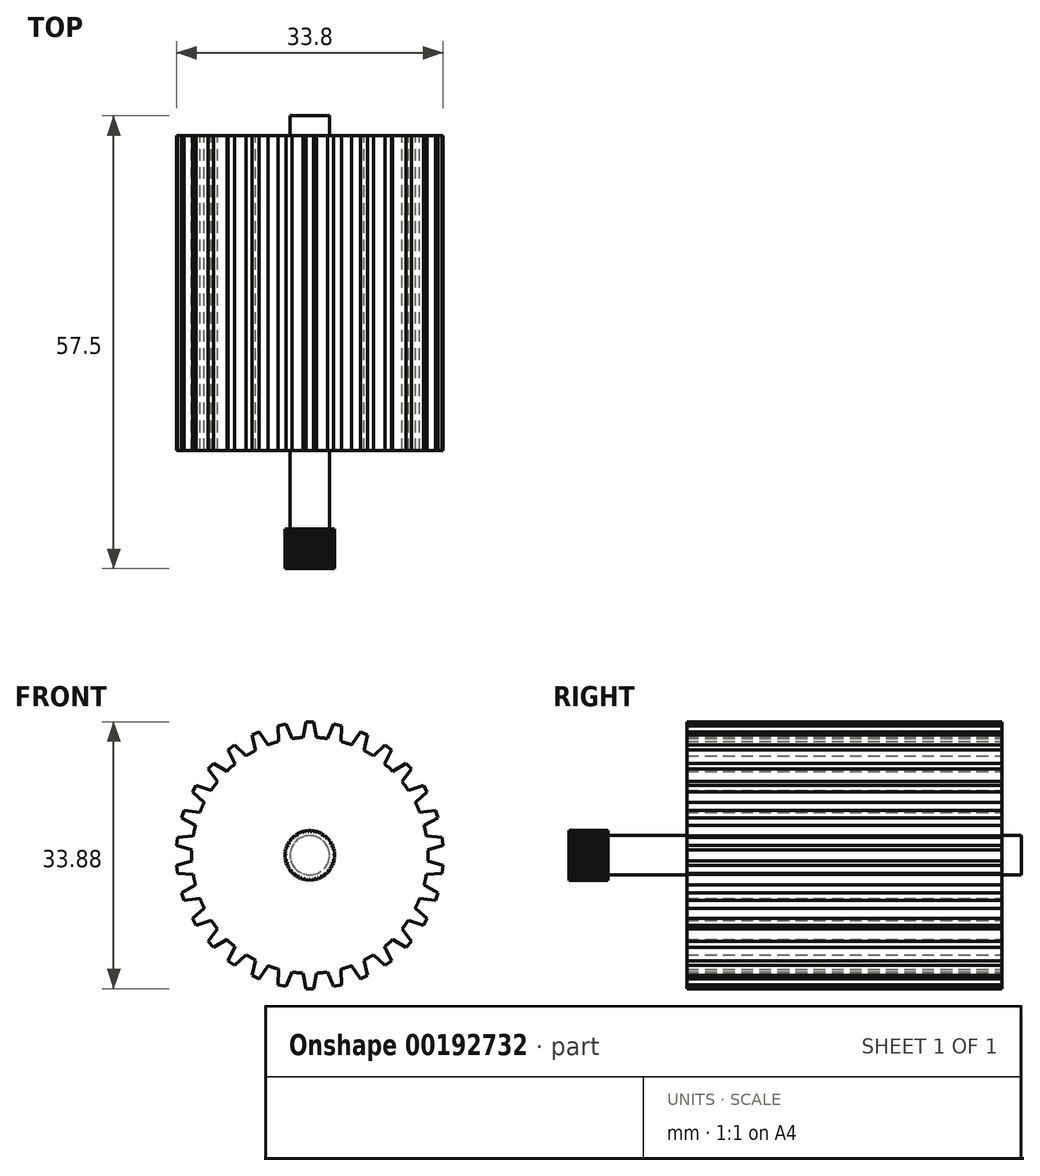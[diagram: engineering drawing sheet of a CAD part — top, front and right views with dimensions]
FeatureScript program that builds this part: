
annotation { "Feature Type Name" : "Feature", "Feature Type Description" : "" }
export const myFeature = defineFeature(function(context is Context, id is Id, definition is map)
    precondition{}
    {
        {
            var Q0;
            Q0=qCreatedBy(makeId("Front.planeOp"),FACE);
            var sketch = newSketch(context, id + "F0", { "sketchPlane" : qUnion([Q0])});
            skCircle(sketch, "E0", {"center": v(0, 0) * mm, "radius": 15 * mm});
            skLineSegment(sketch, "E1", {"start": v(0, 0) * mm, "end": v(0, 16.94) * mm, "construction": true});
            skLineSegment(sketch, "E2", {"start": v(0, 16.94) * mm, "end": v(-0.5, 16.94) * mm});
            skLineSegment(sketch, "E3", {"start": v(-0.5, 16.94) * mm, "end": v(-0.88, 14.97) * mm});
            skLineSegment(sketch, "E4.MirrorCS", {"start": v(0, 16.94) * mm, "end": v(0.5, 16.94) * mm});
            skLineSegment(sketch, "E5.MirrorCS", {"start": v(0.5, 16.94) * mm, "end": v(0.88, 14.97) * mm});
            skLineSegment(sketch, "E6.1.0", {"start": v(-4.01, 16.46) * mm, "end": v(-3.98, 14.46) * mm});
            skLineSegment(sketch, "E6.1.1", {"start": v(-3.52, 16.57) * mm, "end": v(-4.01, 16.46) * mm});
            skLineSegment(sketch, "E6.1.2", {"start": v(-3.52, 16.57) * mm, "end": v(-3.03, 16.67) * mm});
            skLineSegment(sketch, "E6.1.3", {"start": v(-3.03, 16.67) * mm, "end": v(-2.25, 14.83) * mm});
            skLineSegment(sketch, "E6.2.0", {"start": v(-7.35, 15.27) * mm, "end": v(-6.9, 13.32) * mm});
            skLineSegment(sketch, "E6.2.1", {"start": v(-6.89, 15.47) * mm, "end": v(-7.35, 15.27) * mm});
            skLineSegment(sketch, "E6.2.2", {"start": v(-6.89, 15.47) * mm, "end": v(-6.43, 15.68) * mm});
            skLineSegment(sketch, "E6.2.3", {"start": v(-6.43, 15.68) * mm, "end": v(-5.28, 14.04) * mm});
            skLineSegment(sketch, "E7.2.3.0", {"start": v(-10.36, 13.4) * mm, "end": v(-9.52, 11.6) * mm});
            skLineSegment(sketch, "E7.3.3.0", {"start": v(-9.96, 13.7) * mm, "end": v(-10.36, 13.4) * mm});
            skLineSegment(sketch, "E7.6.3.0", {"start": v(-9.96, 13.7) * mm, "end": v(-9.55, 14) * mm});
            skLineSegment(sketch, "E7.9.3.0", {"start": v(-9.55, 14) * mm, "end": v(-8.09, 12.63) * mm});
            skLineSegment(sketch, "E7.2.4.0", {"start": v(-12.92, 10.96) * mm, "end": v(-11.72, 9.36) * mm});
            skLineSegment(sketch, "E7.3.4.0", {"start": v(-12.59, 11.33) * mm, "end": v(-12.92, 10.96) * mm});
            skLineSegment(sketch, "E7.6.4.0", {"start": v(-12.59, 11.33) * mm, "end": v(-12.25, 11.7) * mm});
            skLineSegment(sketch, "E7.9.4.0", {"start": v(-12.25, 11.7) * mm, "end": v(-10.54, 10.68) * mm});
            skLineSegment(sketch, "E7.2.5.0", {"start": v(-14.92, 8.04) * mm, "end": v(-13.4, 6.72) * mm});
            skLineSegment(sketch, "E7.3.5.0", {"start": v(-14.67, 8.47) * mm, "end": v(-14.92, 8.04) * mm});
            skLineSegment(sketch, "E7.6.5.0", {"start": v(-14.67, 8.47) * mm, "end": v(-14.42, 8.9) * mm});
            skLineSegment(sketch, "E7.9.5.0", {"start": v(-14.42, 8.9) * mm, "end": v(-12.53, 8.25) * mm});
            skLineSegment(sketch, "E7.2.6.0", {"start": v(-16.26, 4.76) * mm, "end": v(-14.51, 3.79) * mm});
            skLineSegment(sketch, "E7.3.6.0", {"start": v(-16.1, 5.23) * mm, "end": v(-16.26, 4.76) * mm});
            skLineSegment(sketch, "E7.6.6.0", {"start": v(-16.1, 5.23) * mm, "end": v(-15.95, 5.7) * mm});
            skLineSegment(sketch, "E7.9.6.0", {"start": v(-15.95, 5.7) * mm, "end": v(-13.97, 5.47) * mm});
            skLineSegment(sketch, "E7.2.7.0", {"start": v(-16.9, 1.27) * mm, "end": v(-14.98, 0.69) * mm});
            skLineSegment(sketch, "E7.3.7.0", {"start": v(-16.84, 1.77) * mm, "end": v(-16.9, 1.27) * mm});
            skLineSegment(sketch, "E7.6.7.0", {"start": v(-16.84, 1.77) * mm, "end": v(-16.8, 2.27) * mm});
            skLineSegment(sketch, "E7.9.7.0", {"start": v(-16.8, 2.27) * mm, "end": v(-14.8, 2.44) * mm});
            skLineSegment(sketch, "E7.2.8.0", {"start": v(-16.8, -2.27) * mm, "end": v(-14.8, -2.44) * mm});
            skLineSegment(sketch, "E7.3.8.0", {"start": v(-16.84, -1.77) * mm, "end": v(-16.8, -2.27) * mm});
            skLineSegment(sketch, "E7.6.8.0", {"start": v(-16.84, -1.77) * mm, "end": v(-16.9, -1.27) * mm});
            skLineSegment(sketch, "E7.9.8.0", {"start": v(-16.9, -1.27) * mm, "end": v(-14.98, -0.69) * mm});
            skLineSegment(sketch, "E7.2.9.0", {"start": v(-15.95, -5.7) * mm, "end": v(-13.97, -5.47) * mm});
            skLineSegment(sketch, "E7.3.9.0", {"start": v(-16.1, -5.23) * mm, "end": v(-15.95, -5.7) * mm});
            skLineSegment(sketch, "E7.6.9.0", {"start": v(-16.1, -5.23) * mm, "end": v(-16.26, -4.76) * mm});
            skLineSegment(sketch, "E7.9.9.0", {"start": v(-16.26, -4.76) * mm, "end": v(-14.51, -3.79) * mm});
            skLineSegment(sketch, "E7.2.10.0", {"start": v(-14.42, -8.9) * mm, "end": v(-12.53, -8.25) * mm});
            skLineSegment(sketch, "E7.3.10.0", {"start": v(-14.67, -8.47) * mm, "end": v(-14.42, -8.9) * mm});
            skLineSegment(sketch, "E7.6.10.0", {"start": v(-14.67, -8.47) * mm, "end": v(-14.92, -8.04) * mm});
            skLineSegment(sketch, "E7.9.10.0", {"start": v(-14.92, -8.04) * mm, "end": v(-13.4, -6.72) * mm});
            skLineSegment(sketch, "E7.2.11.0", {"start": v(-12.25, -11.7) * mm, "end": v(-10.54, -10.68) * mm});
            skLineSegment(sketch, "E7.3.11.0", {"start": v(-12.59, -11.33) * mm, "end": v(-12.25, -11.7) * mm});
            skLineSegment(sketch, "E7.6.11.0", {"start": v(-12.59, -11.33) * mm, "end": v(-12.92, -10.96) * mm});
            skLineSegment(sketch, "E7.9.11.0", {"start": v(-12.92, -10.96) * mm, "end": v(-11.72, -9.36) * mm});
            skLineSegment(sketch, "E7.2.12.0", {"start": v(-9.55, -14) * mm, "end": v(-8.09, -12.63) * mm});
            skLineSegment(sketch, "E7.3.12.0", {"start": v(-9.96, -13.7) * mm, "end": v(-9.55, -14) * mm});
            skLineSegment(sketch, "E7.6.12.0", {"start": v(-9.96, -13.7) * mm, "end": v(-10.36, -13.4) * mm});
            skLineSegment(sketch, "E7.9.12.0", {"start": v(-10.36, -13.4) * mm, "end": v(-9.52, -11.6) * mm});
            skLineSegment(sketch, "E7.2.13.0", {"start": v(-6.43, -15.68) * mm, "end": v(-5.28, -14.04) * mm});
            skLineSegment(sketch, "E7.3.13.0", {"start": v(-6.89, -15.47) * mm, "end": v(-6.43, -15.68) * mm});
            skLineSegment(sketch, "E7.6.13.0", {"start": v(-6.89, -15.47) * mm, "end": v(-7.35, -15.27) * mm});
            skLineSegment(sketch, "E7.9.13.0", {"start": v(-7.35, -15.27) * mm, "end": v(-6.9, -13.32) * mm});
            skLineSegment(sketch, "E7.2.14.0", {"start": v(-3.03, -16.67) * mm, "end": v(-2.25, -14.83) * mm});
            skLineSegment(sketch, "E7.3.14.0", {"start": v(-3.52, -16.57) * mm, "end": v(-3.03, -16.67) * mm});
            skLineSegment(sketch, "E7.6.14.0", {"start": v(-3.52, -16.57) * mm, "end": v(-4.01, -16.46) * mm});
            skLineSegment(sketch, "E7.9.14.0", {"start": v(-4.01, -16.46) * mm, "end": v(-3.98, -14.46) * mm});
            skLineSegment(sketch, "E8.2.15.0", {"start": v(0.5, -16.94) * mm, "end": v(0.88, -14.97) * mm});
            skLineSegment(sketch, "E8.3.15.0", {"start": v(0, -16.94) * mm, "end": v(0.5, -16.94) * mm});
            skLineSegment(sketch, "E8.6.15.0", {"start": v(0, -16.94) * mm, "end": v(-0.5, -16.94) * mm});
            skLineSegment(sketch, "E8.9.15.0", {"start": v(-0.5, -16.94) * mm, "end": v(-0.88, -14.97) * mm});
            skLineSegment(sketch, "E8.2.16.0", {"start": v(4.01, -16.46) * mm, "end": v(3.98, -14.46) * mm});
            skLineSegment(sketch, "E8.3.16.0", {"start": v(3.52, -16.57) * mm, "end": v(4.01, -16.46) * mm});
            skLineSegment(sketch, "E8.6.16.0", {"start": v(3.52, -16.57) * mm, "end": v(3.03, -16.67) * mm});
            skLineSegment(sketch, "E8.9.16.0", {"start": v(3.03, -16.67) * mm, "end": v(2.25, -14.83) * mm});
            skLineSegment(sketch, "E8.2.17.0", {"start": v(7.35, -15.27) * mm, "end": v(6.9, -13.32) * mm});
            skLineSegment(sketch, "E8.3.17.0", {"start": v(6.89, -15.47) * mm, "end": v(7.35, -15.27) * mm});
            skLineSegment(sketch, "E8.6.17.0", {"start": v(6.89, -15.47) * mm, "end": v(6.43, -15.68) * mm});
            skLineSegment(sketch, "E8.9.17.0", {"start": v(6.43, -15.68) * mm, "end": v(5.28, -14.04) * mm});
            skLineSegment(sketch, "E8.2.18.0", {"start": v(10.36, -13.4) * mm, "end": v(9.52, -11.6) * mm});
            skLineSegment(sketch, "E8.3.18.0", {"start": v(9.96, -13.7) * mm, "end": v(10.36, -13.4) * mm});
            skLineSegment(sketch, "E8.6.18.0", {"start": v(9.96, -13.7) * mm, "end": v(9.55, -14) * mm});
            skLineSegment(sketch, "E8.9.18.0", {"start": v(9.55, -14) * mm, "end": v(8.09, -12.63) * mm});
            skLineSegment(sketch, "E8.2.19.0", {"start": v(12.92, -10.96) * mm, "end": v(11.72, -9.36) * mm});
            skLineSegment(sketch, "E8.3.19.0", {"start": v(12.59, -11.33) * mm, "end": v(12.92, -10.96) * mm});
            skLineSegment(sketch, "E8.6.19.0", {"start": v(12.59, -11.33) * mm, "end": v(12.25, -11.7) * mm});
            skLineSegment(sketch, "E8.9.19.0", {"start": v(12.25, -11.7) * mm, "end": v(10.54, -10.68) * mm});
            skLineSegment(sketch, "E8.2.20.0", {"start": v(14.92, -8.04) * mm, "end": v(13.4, -6.72) * mm});
            skLineSegment(sketch, "E8.3.20.0", {"start": v(14.67, -8.47) * mm, "end": v(14.92, -8.04) * mm});
            skLineSegment(sketch, "E8.6.20.0", {"start": v(14.67, -8.47) * mm, "end": v(14.42, -8.9) * mm});
            skLineSegment(sketch, "E8.9.20.0", {"start": v(14.42, -8.9) * mm, "end": v(12.53, -8.25) * mm});
            skLineSegment(sketch, "E8.2.21.0", {"start": v(16.26, -4.76) * mm, "end": v(14.51, -3.79) * mm});
            skLineSegment(sketch, "E8.3.21.0", {"start": v(16.1, -5.23) * mm, "end": v(16.26, -4.76) * mm});
            skLineSegment(sketch, "E8.6.21.0", {"start": v(16.1, -5.23) * mm, "end": v(15.95, -5.7) * mm});
            skLineSegment(sketch, "E8.9.21.0", {"start": v(15.95, -5.7) * mm, "end": v(13.97, -5.47) * mm});
            skLineSegment(sketch, "E8.2.22.0", {"start": v(16.9, -1.27) * mm, "end": v(14.98, -0.69) * mm});
            skLineSegment(sketch, "E8.3.22.0", {"start": v(16.84, -1.77) * mm, "end": v(16.9, -1.27) * mm});
            skLineSegment(sketch, "E8.6.22.0", {"start": v(16.84, -1.77) * mm, "end": v(16.8, -2.27) * mm});
            skLineSegment(sketch, "E8.9.22.0", {"start": v(16.8, -2.27) * mm, "end": v(14.8, -2.44) * mm});
            skLineSegment(sketch, "E8.2.23.0", {"start": v(16.8, 2.27) * mm, "end": v(14.8, 2.44) * mm});
            skLineSegment(sketch, "E8.3.23.0", {"start": v(16.84, 1.77) * mm, "end": v(16.8, 2.27) * mm});
            skLineSegment(sketch, "E8.6.23.0", {"start": v(16.84, 1.77) * mm, "end": v(16.9, 1.27) * mm});
            skLineSegment(sketch, "E8.9.23.0", {"start": v(16.9, 1.27) * mm, "end": v(14.98, 0.69) * mm});
            skLineSegment(sketch, "E8.2.24.0", {"start": v(15.95, 5.7) * mm, "end": v(13.97, 5.47) * mm});
            skLineSegment(sketch, "E8.3.24.0", {"start": v(16.1, 5.23) * mm, "end": v(15.95, 5.7) * mm});
            skLineSegment(sketch, "E8.6.24.0", {"start": v(16.1, 5.23) * mm, "end": v(16.26, 4.76) * mm});
            skLineSegment(sketch, "E8.9.24.0", {"start": v(16.26, 4.76) * mm, "end": v(14.51, 3.79) * mm});
            skLineSegment(sketch, "E9.2.25.0", {"start": v(14.42, 8.9) * mm, "end": v(12.53, 8.25) * mm});
            skLineSegment(sketch, "E9.3.25.0", {"start": v(14.67, 8.47) * mm, "end": v(14.42, 8.9) * mm});
            skLineSegment(sketch, "E9.6.25.0", {"start": v(14.67, 8.47) * mm, "end": v(14.92, 8.04) * mm});
            skLineSegment(sketch, "E9.9.25.0", {"start": v(14.92, 8.04) * mm, "end": v(13.4, 6.72) * mm});
            skLineSegment(sketch, "E9.2.26.0", {"start": v(12.25, 11.7) * mm, "end": v(10.54, 10.68) * mm});
            skLineSegment(sketch, "E9.3.26.0", {"start": v(12.59, 11.33) * mm, "end": v(12.25, 11.7) * mm});
            skLineSegment(sketch, "E9.6.26.0", {"start": v(12.59, 11.33) * mm, "end": v(12.92, 10.96) * mm});
            skLineSegment(sketch, "E9.9.26.0", {"start": v(12.92, 10.96) * mm, "end": v(11.72, 9.36) * mm});
            skLineSegment(sketch, "E9.2.27.0", {"start": v(9.55, 14) * mm, "end": v(8.09, 12.63) * mm});
            skLineSegment(sketch, "E9.3.27.0", {"start": v(9.96, 13.7) * mm, "end": v(9.55, 14) * mm});
            skLineSegment(sketch, "E9.6.27.0", {"start": v(9.96, 13.7) * mm, "end": v(10.36, 13.4) * mm});
            skLineSegment(sketch, "E9.9.27.0", {"start": v(10.36, 13.4) * mm, "end": v(9.52, 11.6) * mm});
            skLineSegment(sketch, "E9.2.28.0", {"start": v(6.43, 15.68) * mm, "end": v(5.28, 14.04) * mm});
            skLineSegment(sketch, "E9.3.28.0", {"start": v(6.89, 15.47) * mm, "end": v(6.43, 15.68) * mm});
            skLineSegment(sketch, "E9.6.28.0", {"start": v(6.89, 15.47) * mm, "end": v(7.35, 15.27) * mm});
            skLineSegment(sketch, "E9.9.28.0", {"start": v(7.35, 15.27) * mm, "end": v(6.9, 13.32) * mm});
            skLineSegment(sketch, "E9.2.29.0", {"start": v(3.03, 16.67) * mm, "end": v(2.25, 14.83) * mm});
            skLineSegment(sketch, "E9.3.29.0", {"start": v(3.52, 16.57) * mm, "end": v(3.03, 16.67) * mm});
            skLineSegment(sketch, "E9.6.29.0", {"start": v(3.52, 16.57) * mm, "end": v(4.01, 16.46) * mm});
            skLineSegment(sketch, "E9.9.29.0", {"start": v(4.01, 16.46) * mm, "end": v(3.98, 14.46) * mm});
            skSolve(sketch);
        }
        {
            var Q0;
            Q0=qSketchRegion(id+"F0",true);
            extrude(context, id + "F1", {"entities" : qUnion([Q0]), "depth" : 40 * mm});
        }
        {
            var Q0;
            Q0=makeQuery(id+"F1.opExtrude","CAP_FACE",FACE,{"disambiguationData":[OSD([sQuery(id+"F0.wireOp",EDGE,"E0"),sQuery(id+"F0.wireOp",EDGE,"E2"),sQuery(id+"F0.wireOp",EDGE,"E3"),sQuery(id+"F0.wireOp",EDGE,"E4.MirrorCS"),sQuery(id+"F0.wireOp",EDGE,"E5.MirrorCS"),sQuery(id+"F0.wireOp",EDGE,"E6.1.0"),sQuery(id+"F0.wireOp",EDGE,"E6.1.1"),sQuery(id+"F0.wireOp",EDGE,"E6.1.2"),sQuery(id+"F0.wireOp",EDGE,"E6.1.3"),sQuery(id+"F0.wireOp",EDGE,"E6.2.0"),sQuery(id+"F0.wireOp",EDGE,"E6.2.1"),sQuery(id+"F0.wireOp",EDGE,"E6.2.2"),sQuery(id+"F0.wireOp",EDGE,"E6.2.3"),sQuery(id+"F0.wireOp",EDGE,"E7.2.3.0"),sQuery(id+"F0.wireOp",EDGE,"E7.3.3.0"),sQuery(id+"F0.wireOp",EDGE,"E7.6.3.0"),sQuery(id+"F0.wireOp",EDGE,"E7.9.3.0"),sQuery(id+"F0.wireOp",EDGE,"E7.2.4.0"),sQuery(id+"F0.wireOp",EDGE,"E7.3.4.0"),sQuery(id+"F0.wireOp",EDGE,"E7.6.4.0"),sQuery(id+"F0.wireOp",EDGE,"E7.9.4.0"),sQuery(id+"F0.wireOp",EDGE,"E7.2.5.0"),sQuery(id+"F0.wireOp",EDGE,"E7.3.5.0"),sQuery(id+"F0.wireOp",EDGE,"E7.6.5.0"),sQuery(id+"F0.wireOp",EDGE,"E7.9.5.0"),sQuery(id+"F0.wireOp",EDGE,"E7.2.6.0"),sQuery(id+"F0.wireOp",EDGE,"E7.3.6.0"),sQuery(id+"F0.wireOp",EDGE,"E7.6.6.0"),sQuery(id+"F0.wireOp",EDGE,"E7.9.6.0"),sQuery(id+"F0.wireOp",EDGE,"E7.2.7.0"),sQuery(id+"F0.wireOp",EDGE,"E7.3.7.0"),sQuery(id+"F0.wireOp",EDGE,"E7.6.7.0"),sQuery(id+"F0.wireOp",EDGE,"E7.9.7.0"),sQuery(id+"F0.wireOp",EDGE,"E7.2.8.0"),sQuery(id+"F0.wireOp",EDGE,"E7.3.8.0"),sQuery(id+"F0.wireOp",EDGE,"E7.6.8.0"),sQuery(id+"F0.wireOp",EDGE,"E7.9.8.0"),sQuery(id+"F0.wireOp",EDGE,"E7.2.9.0"),sQuery(id+"F0.wireOp",EDGE,"E7.3.9.0"),sQuery(id+"F0.wireOp",EDGE,"E7.6.9.0"),sQuery(id+"F0.wireOp",EDGE,"E7.9.9.0"),sQuery(id+"F0.wireOp",EDGE,"E7.2.10.0"),sQuery(id+"F0.wireOp",EDGE,"E7.3.10.0"),sQuery(id+"F0.wireOp",EDGE,"E7.6.10.0"),sQuery(id+"F0.wireOp",EDGE,"E7.9.10.0"),sQuery(id+"F0.wireOp",EDGE,"E7.2.11.0"),sQuery(id+"F0.wireOp",EDGE,"E7.3.11.0"),sQuery(id+"F0.wireOp",EDGE,"E7.6.11.0"),sQuery(id+"F0.wireOp",EDGE,"E7.9.11.0"),sQuery(id+"F0.wireOp",EDGE,"E7.2.12.0"),sQuery(id+"F0.wireOp",EDGE,"E7.3.12.0"),sQuery(id+"F0.wireOp",EDGE,"E7.6.12.0"),sQuery(id+"F0.wireOp",EDGE,"E7.9.12.0"),sQuery(id+"F0.wireOp",EDGE,"E7.2.13.0"),sQuery(id+"F0.wireOp",EDGE,"E7.3.13.0"),sQuery(id+"F0.wireOp",EDGE,"E7.6.13.0"),sQuery(id+"F0.wireOp",EDGE,"E7.9.13.0"),sQuery(id+"F0.wireOp",EDGE,"E7.2.14.0"),sQuery(id+"F0.wireOp",EDGE,"E7.3.14.0"),sQuery(id+"F0.wireOp",EDGE,"E7.6.14.0"),sQuery(id+"F0.wireOp",EDGE,"E7.9.14.0"),sQuery(id+"F0.wireOp",EDGE,"E8.2.15.0"),sQuery(id+"F0.wireOp",EDGE,"E8.3.15.0"),sQuery(id+"F0.wireOp",EDGE,"E8.6.15.0"),sQuery(id+"F0.wireOp",EDGE,"E8.9.15.0"),sQuery(id+"F0.wireOp",EDGE,"E8.2.16.0"),sQuery(id+"F0.wireOp",EDGE,"E8.3.16.0"),sQuery(id+"F0.wireOp",EDGE,"E8.6.16.0"),sQuery(id+"F0.wireOp",EDGE,"E8.9.16.0"),sQuery(id+"F0.wireOp",EDGE,"E8.2.17.0"),sQuery(id+"F0.wireOp",EDGE,"E8.3.17.0"),sQuery(id+"F0.wireOp",EDGE,"E8.6.17.0"),sQuery(id+"F0.wireOp",EDGE,"E8.9.17.0"),sQuery(id+"F0.wireOp",EDGE,"E8.2.18.0"),sQuery(id+"F0.wireOp",EDGE,"E8.3.18.0"),sQuery(id+"F0.wireOp",EDGE,"E8.6.18.0"),sQuery(id+"F0.wireOp",EDGE,"E8.9.18.0"),sQuery(id+"F0.wireOp",EDGE,"E8.2.19.0"),sQuery(id+"F0.wireOp",EDGE,"E8.3.19.0"),sQuery(id+"F0.wireOp",EDGE,"E8.6.19.0"),sQuery(id+"F0.wireOp",EDGE,"E8.9.19.0"),sQuery(id+"F0.wireOp",EDGE,"E8.2.20.0"),sQuery(id+"F0.wireOp",EDGE,"E8.3.20.0"),sQuery(id+"F0.wireOp",EDGE,"E8.6.20.0"),sQuery(id+"F0.wireOp",EDGE,"E8.9.20.0"),sQuery(id+"F0.wireOp",EDGE,"E8.2.21.0"),sQuery(id+"F0.wireOp",EDGE,"E8.3.21.0"),sQuery(id+"F0.wireOp",EDGE,"E8.6.21.0"),sQuery(id+"F0.wireOp",EDGE,"E8.9.21.0"),sQuery(id+"F0.wireOp",EDGE,"E8.2.22.0"),sQuery(id+"F0.wireOp",EDGE,"E8.3.22.0"),sQuery(id+"F0.wireOp",EDGE,"E8.6.22.0"),sQuery(id+"F0.wireOp",EDGE,"E8.9.22.0"),sQuery(id+"F0.wireOp",EDGE,"E8.2.23.0"),sQuery(id+"F0.wireOp",EDGE,"E8.3.23.0"),sQuery(id+"F0.wireOp",EDGE,"E8.6.23.0"),sQuery(id+"F0.wireOp",EDGE,"E8.9.23.0"),sQuery(id+"F0.wireOp",EDGE,"E8.2.24.0"),sQuery(id+"F0.wireOp",EDGE,"E8.3.24.0"),sQuery(id+"F0.wireOp",EDGE,"E8.6.24.0"),sQuery(id+"F0.wireOp",EDGE,"E8.9.24.0"),sQuery(id+"F0.wireOp",EDGE,"E9.2.25.0"),sQuery(id+"F0.wireOp",EDGE,"E9.3.25.0"),sQuery(id+"F0.wireOp",EDGE,"E9.6.25.0"),sQuery(id+"F0.wireOp",EDGE,"E9.9.25.0"),sQuery(id+"F0.wireOp",EDGE,"E9.2.26.0"),sQuery(id+"F0.wireOp",EDGE,"E9.3.26.0"),sQuery(id+"F0.wireOp",EDGE,"E9.6.26.0"),sQuery(id+"F0.wireOp",EDGE,"E9.9.26.0"),sQuery(id+"F0.wireOp",EDGE,"E9.2.27.0"),sQuery(id+"F0.wireOp",EDGE,"E9.3.27.0"),sQuery(id+"F0.wireOp",EDGE,"E9.6.27.0"),sQuery(id+"F0.wireOp",EDGE,"E9.9.27.0"),sQuery(id+"F0.wireOp",EDGE,"E9.2.28.0"),sQuery(id+"F0.wireOp",EDGE,"E9.3.28.0"),sQuery(id+"F0.wireOp",EDGE,"E9.6.28.0"),sQuery(id+"F0.wireOp",EDGE,"E9.9.28.0"),sQuery(id+"F0.wireOp",EDGE,"E9.2.29.0"),sQuery(id+"F0.wireOp",EDGE,"E9.3.29.0"),sQuery(id+"F0.wireOp",EDGE,"E9.6.29.0"),sQuery(id+"F0.wireOp",EDGE,"E9.9.29.0")])],"isStart":false});
            var sketch = newSketch(context, id + "F2", { "sketchPlane" : qUnion([Q0])});
            skCircle(sketch, "E10", {"center": v(0, 0) * mm, "radius": 2.5 * mm});
            skSolve(sketch);
        }
        {
            var Q0;
            Q0 = qSketchRegion(id + "F2", true);
            extrude(context, id + "F3", {"entities" : qUnion([Q0]), "operationType" : NewBodyOperationType.ADD, "depth" : 15 * mm});
        }
        {
            var Q0;
            Q0=makeQuery(id+"F1.opExtrude","CAP_FACE",FACE,{"disambiguationData":[OSD([sQuery(id+"F0.wireOp",EDGE,"E0"),sQuery(id+"F0.wireOp",EDGE,"E2"),sQuery(id+"F0.wireOp",EDGE,"E3"),sQuery(id+"F0.wireOp",EDGE,"E4.MirrorCS"),sQuery(id+"F0.wireOp",EDGE,"E5.MirrorCS"),sQuery(id+"F0.wireOp",EDGE,"E6.1.0"),sQuery(id+"F0.wireOp",EDGE,"E6.1.1"),sQuery(id+"F0.wireOp",EDGE,"E6.1.2"),sQuery(id+"F0.wireOp",EDGE,"E6.1.3"),sQuery(id+"F0.wireOp",EDGE,"E6.2.0"),sQuery(id+"F0.wireOp",EDGE,"E6.2.1"),sQuery(id+"F0.wireOp",EDGE,"E6.2.2"),sQuery(id+"F0.wireOp",EDGE,"E6.2.3"),sQuery(id+"F0.wireOp",EDGE,"E7.2.3.0"),sQuery(id+"F0.wireOp",EDGE,"E7.3.3.0"),sQuery(id+"F0.wireOp",EDGE,"E7.6.3.0"),sQuery(id+"F0.wireOp",EDGE,"E7.9.3.0"),sQuery(id+"F0.wireOp",EDGE,"E7.2.4.0"),sQuery(id+"F0.wireOp",EDGE,"E7.3.4.0"),sQuery(id+"F0.wireOp",EDGE,"E7.6.4.0"),sQuery(id+"F0.wireOp",EDGE,"E7.9.4.0"),sQuery(id+"F0.wireOp",EDGE,"E7.2.5.0"),sQuery(id+"F0.wireOp",EDGE,"E7.3.5.0"),sQuery(id+"F0.wireOp",EDGE,"E7.6.5.0"),sQuery(id+"F0.wireOp",EDGE,"E7.9.5.0"),sQuery(id+"F0.wireOp",EDGE,"E7.2.6.0"),sQuery(id+"F0.wireOp",EDGE,"E7.3.6.0"),sQuery(id+"F0.wireOp",EDGE,"E7.6.6.0"),sQuery(id+"F0.wireOp",EDGE,"E7.9.6.0"),sQuery(id+"F0.wireOp",EDGE,"E7.2.7.0"),sQuery(id+"F0.wireOp",EDGE,"E7.3.7.0"),sQuery(id+"F0.wireOp",EDGE,"E7.6.7.0"),sQuery(id+"F0.wireOp",EDGE,"E7.9.7.0"),sQuery(id+"F0.wireOp",EDGE,"E7.2.8.0"),sQuery(id+"F0.wireOp",EDGE,"E7.3.8.0"),sQuery(id+"F0.wireOp",EDGE,"E7.6.8.0"),sQuery(id+"F0.wireOp",EDGE,"E7.9.8.0"),sQuery(id+"F0.wireOp",EDGE,"E7.2.9.0"),sQuery(id+"F0.wireOp",EDGE,"E7.3.9.0"),sQuery(id+"F0.wireOp",EDGE,"E7.6.9.0"),sQuery(id+"F0.wireOp",EDGE,"E7.9.9.0"),sQuery(id+"F0.wireOp",EDGE,"E7.2.10.0"),sQuery(id+"F0.wireOp",EDGE,"E7.3.10.0"),sQuery(id+"F0.wireOp",EDGE,"E7.6.10.0"),sQuery(id+"F0.wireOp",EDGE,"E7.9.10.0"),sQuery(id+"F0.wireOp",EDGE,"E7.2.11.0"),sQuery(id+"F0.wireOp",EDGE,"E7.3.11.0"),sQuery(id+"F0.wireOp",EDGE,"E7.6.11.0"),sQuery(id+"F0.wireOp",EDGE,"E7.9.11.0"),sQuery(id+"F0.wireOp",EDGE,"E7.2.12.0"),sQuery(id+"F0.wireOp",EDGE,"E7.3.12.0"),sQuery(id+"F0.wireOp",EDGE,"E7.6.12.0"),sQuery(id+"F0.wireOp",EDGE,"E7.9.12.0"),sQuery(id+"F0.wireOp",EDGE,"E7.2.13.0"),sQuery(id+"F0.wireOp",EDGE,"E7.3.13.0"),sQuery(id+"F0.wireOp",EDGE,"E7.6.13.0"),sQuery(id+"F0.wireOp",EDGE,"E7.9.13.0"),sQuery(id+"F0.wireOp",EDGE,"E7.2.14.0"),sQuery(id+"F0.wireOp",EDGE,"E7.3.14.0"),sQuery(id+"F0.wireOp",EDGE,"E7.6.14.0"),sQuery(id+"F0.wireOp",EDGE,"E7.9.14.0"),sQuery(id+"F0.wireOp",EDGE,"E8.2.15.0"),sQuery(id+"F0.wireOp",EDGE,"E8.3.15.0"),sQuery(id+"F0.wireOp",EDGE,"E8.6.15.0"),sQuery(id+"F0.wireOp",EDGE,"E8.9.15.0"),sQuery(id+"F0.wireOp",EDGE,"E8.2.16.0"),sQuery(id+"F0.wireOp",EDGE,"E8.3.16.0"),sQuery(id+"F0.wireOp",EDGE,"E8.6.16.0"),sQuery(id+"F0.wireOp",EDGE,"E8.9.16.0"),sQuery(id+"F0.wireOp",EDGE,"E8.2.17.0"),sQuery(id+"F0.wireOp",EDGE,"E8.3.17.0"),sQuery(id+"F0.wireOp",EDGE,"E8.6.17.0"),sQuery(id+"F0.wireOp",EDGE,"E8.9.17.0"),sQuery(id+"F0.wireOp",EDGE,"E8.2.18.0"),sQuery(id+"F0.wireOp",EDGE,"E8.3.18.0"),sQuery(id+"F0.wireOp",EDGE,"E8.6.18.0"),sQuery(id+"F0.wireOp",EDGE,"E8.9.18.0"),sQuery(id+"F0.wireOp",EDGE,"E8.2.19.0"),sQuery(id+"F0.wireOp",EDGE,"E8.3.19.0"),sQuery(id+"F0.wireOp",EDGE,"E8.6.19.0"),sQuery(id+"F0.wireOp",EDGE,"E8.9.19.0"),sQuery(id+"F0.wireOp",EDGE,"E8.2.20.0"),sQuery(id+"F0.wireOp",EDGE,"E8.3.20.0"),sQuery(id+"F0.wireOp",EDGE,"E8.6.20.0"),sQuery(id+"F0.wireOp",EDGE,"E8.9.20.0"),sQuery(id+"F0.wireOp",EDGE,"E8.2.21.0"),sQuery(id+"F0.wireOp",EDGE,"E8.3.21.0"),sQuery(id+"F0.wireOp",EDGE,"E8.6.21.0"),sQuery(id+"F0.wireOp",EDGE,"E8.9.21.0"),sQuery(id+"F0.wireOp",EDGE,"E8.2.22.0"),sQuery(id+"F0.wireOp",EDGE,"E8.3.22.0"),sQuery(id+"F0.wireOp",EDGE,"E8.6.22.0"),sQuery(id+"F0.wireOp",EDGE,"E8.9.22.0"),sQuery(id+"F0.wireOp",EDGE,"E8.2.23.0"),sQuery(id+"F0.wireOp",EDGE,"E8.3.23.0"),sQuery(id+"F0.wireOp",EDGE,"E8.6.23.0"),sQuery(id+"F0.wireOp",EDGE,"E8.9.23.0"),sQuery(id+"F0.wireOp",EDGE,"E8.2.24.0"),sQuery(id+"F0.wireOp",EDGE,"E8.3.24.0"),sQuery(id+"F0.wireOp",EDGE,"E8.6.24.0"),sQuery(id+"F0.wireOp",EDGE,"E8.9.24.0"),sQuery(id+"F0.wireOp",EDGE,"E9.2.25.0"),sQuery(id+"F0.wireOp",EDGE,"E9.3.25.0"),sQuery(id+"F0.wireOp",EDGE,"E9.6.25.0"),sQuery(id+"F0.wireOp",EDGE,"E9.9.25.0"),sQuery(id+"F0.wireOp",EDGE,"E9.2.26.0"),sQuery(id+"F0.wireOp",EDGE,"E9.3.26.0"),sQuery(id+"F0.wireOp",EDGE,"E9.6.26.0"),sQuery(id+"F0.wireOp",EDGE,"E9.9.26.0"),sQuery(id+"F0.wireOp",EDGE,"E9.2.27.0"),sQuery(id+"F0.wireOp",EDGE,"E9.3.27.0"),sQuery(id+"F0.wireOp",EDGE,"E9.6.27.0"),sQuery(id+"F0.wireOp",EDGE,"E9.9.27.0"),sQuery(id+"F0.wireOp",EDGE,"E9.2.28.0"),sQuery(id+"F0.wireOp",EDGE,"E9.3.28.0"),sQuery(id+"F0.wireOp",EDGE,"E9.6.28.0"),sQuery(id+"F0.wireOp",EDGE,"E9.9.28.0"),sQuery(id+"F0.wireOp",EDGE,"E9.2.29.0"),sQuery(id+"F0.wireOp",EDGE,"E9.3.29.0"),sQuery(id+"F0.wireOp",EDGE,"E9.6.29.0"),sQuery(id+"F0.wireOp",EDGE,"E9.9.29.0")])],"isStart":true});
            var sketch = newSketch(context, id + "F4", { "sketchPlane" : qUnion([Q0])});
            skCircle(sketch, "E11", {"center": v(0, 0) * mm, "radius": 2.5 * mm});
            skSolve(sketch);
        }
        {
            var Q0;
            Q0 = qSketchRegion(id + "F4", true);
            extrude(context, id + "F5", {"entities" : qUnion([Q0]), "operationType" : NewBodyOperationType.ADD, "depth" : 2.5 * mm});
        }
        {
            var Q0;
            Q0=makeQuery(id+"F3.opExtrude","CAP_FACE",FACE,{"disambiguationData":[OSD([sQuery(id+"F2.wireOp",EDGE,"E10")])],"isStart":false});
            var sketch = newSketch(context, id + "F6", { "sketchPlane" : qUnion([Q0])});
            skCircle(sketch, "E12", {"center": v(0, 0) * mm, "radius": 3 * mm});
            skLineSegment(sketch, "E13", {"start": v(0, 0) * mm, "end": v(0, 5.06) * mm, "construction": true});
            skLineSegment(sketch, "E14.bottom", {"start": v(0.15, 3.15) * mm, "end": v(-0.15, 3.15) * mm});
            skLineSegment(sketch, "E14.top", {"start": v(0.15, 2.85) * mm, "end": v(-0.15, 2.85) * mm});
            skLineSegment(sketch, "E14.left", {"start": v(0.15, 3.15) * mm, "end": v(0.15, 2.85) * mm});
            skLineSegment(sketch, "E14.right", {"start": v(-0.15, 3.15) * mm, "end": v(-0.15, 2.85) * mm});
            skPoint(sketch, "E14.middle", {"position": v(0, 3) * mm});
            skLineSegment(sketch, "E15.1.0", {"start": v(-0.21, 3.15) * mm, "end": v(-0.18, 2.85) * mm});
            skLineSegment(sketch, "E15.1.1", {"start": v(-0.21, 3.15) * mm, "end": v(-0.5, 3.11) * mm});
            skLineSegment(sketch, "E15.1.2", {"start": v(-0.5, 3.11) * mm, "end": v(-0.47, 2.81) * mm});
            skLineSegment(sketch, "E15.1.3", {"start": v(-0.18, 2.85) * mm, "end": v(-0.47, 2.81) * mm});
            skLineSegment(sketch, "E15.2.0", {"start": v(-0.57, 3.1) * mm, "end": v(-0.5, 2.8) * mm});
            skLineSegment(sketch, "E15.2.1", {"start": v(-0.57, 3.1) * mm, "end": v(-0.86, 3.03) * mm});
            skLineSegment(sketch, "E15.2.2", {"start": v(-0.86, 3.03) * mm, "end": v(-0.8, 2.74) * mm});
            skLineSegment(sketch, "E15.2.3", {"start": v(-0.5, 2.8) * mm, "end": v(-0.8, 2.74) * mm});
            skLineSegment(sketch, "E16.2.3.0", {"start": v(-0.92, 3.02) * mm, "end": v(-0.82, 2.73) * mm});
            skLineSegment(sketch, "E16.3.3.0", {"start": v(-0.92, 3.02) * mm, "end": v(-1.2, 2.92) * mm});
            skLineSegment(sketch, "E16.6.3.0", {"start": v(-1.2, 2.92) * mm, "end": v(-1.1, 2.63) * mm});
            skLineSegment(sketch, "E16.9.3.0", {"start": v(-0.82, 2.73) * mm, "end": v(-1.1, 2.63) * mm});
            skLineSegment(sketch, "E16.2.4.0", {"start": v(-1.26, 2.9) * mm, "end": v(-1.12, 2.62) * mm});
            skLineSegment(sketch, "E16.3.4.0", {"start": v(-1.26, 2.9) * mm, "end": v(-1.52, 2.76) * mm});
            skLineSegment(sketch, "E16.6.4.0", {"start": v(-1.52, 2.76) * mm, "end": v(-1.4, 2.5) * mm});
            skLineSegment(sketch, "E16.9.4.0", {"start": v(-1.12, 2.62) * mm, "end": v(-1.4, 2.5) * mm});
            skLineSegment(sketch, "E16.2.5.0", {"start": v(-1.58, 2.73) * mm, "end": v(-1.41, 2.48) * mm});
            skLineSegment(sketch, "E16.3.5.0", {"start": v(-1.58, 2.73) * mm, "end": v(-1.83, 2.57) * mm});
            skLineSegment(sketch, "E16.6.5.0", {"start": v(-1.83, 2.57) * mm, "end": v(-1.67, 2.32) * mm});
            skLineSegment(sketch, "E16.9.5.0", {"start": v(-1.41, 2.48) * mm, "end": v(-1.67, 2.32) * mm});
            skLineSegment(sketch, "E16.2.6.0", {"start": v(-1.88, 2.53) * mm, "end": v(-1.69, 2.3) * mm});
            skLineSegment(sketch, "E16.3.6.0", {"start": v(-1.88, 2.53) * mm, "end": v(-2.11, 2.34) * mm});
            skLineSegment(sketch, "E16.6.6.0", {"start": v(-2.11, 2.34) * mm, "end": v(-1.92, 2.11) * mm});
            skLineSegment(sketch, "E16.9.6.0", {"start": v(-1.69, 2.3) * mm, "end": v(-1.92, 2.11) * mm});
            skLineSegment(sketch, "E16.2.7.0", {"start": v(-2.15, 2.3) * mm, "end": v(-1.94, 2.1) * mm});
            skLineSegment(sketch, "E16.3.7.0", {"start": v(-2.15, 2.3) * mm, "end": v(-2.36, 2.09) * mm});
            skLineSegment(sketch, "E16.6.7.0", {"start": v(-2.36, 2.09) * mm, "end": v(-2.15, 1.88) * mm});
            skLineSegment(sketch, "E16.9.7.0", {"start": v(-1.94, 2.1) * mm, "end": v(-2.15, 1.88) * mm});
            skLineSegment(sketch, "E16.2.8.0", {"start": v(-2.4, 2.04) * mm, "end": v(-2.17, 1.86) * mm});
            skLineSegment(sketch, "E16.3.8.0", {"start": v(-2.4, 2.04) * mm, "end": v(-2.59, 1.8) * mm});
            skLineSegment(sketch, "E16.6.8.0", {"start": v(-2.59, 1.8) * mm, "end": v(-2.35, 1.62) * mm});
            skLineSegment(sketch, "E16.9.8.0", {"start": v(-2.17, 1.86) * mm, "end": v(-2.35, 1.62) * mm});
            skLineSegment(sketch, "E16.2.9.0", {"start": v(-2.62, 1.76) * mm, "end": v(-2.36, 1.6) * mm});
            skLineSegment(sketch, "E16.3.9.0", {"start": v(-2.62, 1.76) * mm, "end": v(-2.77, 1.5) * mm});
            skLineSegment(sketch, "E16.6.9.0", {"start": v(-2.77, 1.5) * mm, "end": v(-2.52, 1.34) * mm});
            skLineSegment(sketch, "E16.9.9.0", {"start": v(-2.36, 1.6) * mm, "end": v(-2.52, 1.34) * mm});
            skLineSegment(sketch, "E17.2.10.0", {"start": v(-2.8, 1.45) * mm, "end": v(-2.53, 1.32) * mm});
            skLineSegment(sketch, "E17.3.10.0", {"start": v(-2.8, 1.45) * mm, "end": v(-2.93, 1.17) * mm});
            skLineSegment(sketch, "E17.6.10.0", {"start": v(-2.93, 1.17) * mm, "end": v(-2.65, 1.05) * mm});
            skLineSegment(sketch, "E17.9.10.0", {"start": v(-2.53, 1.32) * mm, "end": v(-2.65, 1.05) * mm});
            skLineSegment(sketch, "E17.2.11.0", {"start": v(-2.95, 1.12) * mm, "end": v(-2.66, 1.02) * mm});
            skLineSegment(sketch, "E17.3.11.0", {"start": v(-2.95, 1.12) * mm, "end": v(-3.04, 0.83) * mm});
            skLineSegment(sketch, "E17.6.11.0", {"start": v(-3.04, 0.83) * mm, "end": v(-2.76, 0.74) * mm});
            skLineSegment(sketch, "E17.9.11.0", {"start": v(-2.66, 1.02) * mm, "end": v(-2.76, 0.74) * mm});
            skLineSegment(sketch, "E17.2.12.0", {"start": v(-3.06, 0.77) * mm, "end": v(-2.76, 0.71) * mm});
            skLineSegment(sketch, "E17.3.12.0", {"start": v(-3.06, 0.77) * mm, "end": v(-3.12, 0.48) * mm});
            skLineSegment(sketch, "E17.6.12.0", {"start": v(-3.12, 0.48) * mm, "end": v(-2.82, 0.42) * mm});
            skLineSegment(sketch, "E17.9.12.0", {"start": v(-2.76, 0.71) * mm, "end": v(-2.82, 0.42) * mm});
            skLineSegment(sketch, "E17.2.13.0", {"start": v(-3.13, 0.42) * mm, "end": v(-2.83, 0.4) * mm});
            skLineSegment(sketch, "E17.3.13.0", {"start": v(-3.13, 0.42) * mm, "end": v(-3.15, 0.12) * mm});
            skLineSegment(sketch, "E17.6.13.0", {"start": v(-3.15, 0.12) * mm, "end": v(-2.85, 0.1) * mm});
            skLineSegment(sketch, "E17.9.13.0", {"start": v(-2.83, 0.4) * mm, "end": v(-2.85, 0.1) * mm});
            skLineSegment(sketch, "E17.2.14.0", {"start": v(-3.15, 0.06) * mm, "end": v(-2.85, 0.07) * mm});
            skLineSegment(sketch, "E17.3.14.0", {"start": v(-3.15, 0.06) * mm, "end": v(-3.14, -0.24) * mm});
            skLineSegment(sketch, "E17.6.14.0", {"start": v(-3.14, -0.24) * mm, "end": v(-2.84, -0.23) * mm});
            skLineSegment(sketch, "E17.9.14.0", {"start": v(-2.85, 0.07) * mm, "end": v(-2.84, -0.23) * mm});
            skLineSegment(sketch, "E17.2.15.0", {"start": v(-3.14, -0.3) * mm, "end": v(-2.84, -0.26) * mm});
            skLineSegment(sketch, "E17.3.15.0", {"start": v(-3.14, -0.3) * mm, "end": v(-3.1, -0.6) * mm});
            skLineSegment(sketch, "E17.6.15.0", {"start": v(-3.1, -0.6) * mm, "end": v(-2.8, -0.55) * mm});
            skLineSegment(sketch, "E17.9.15.0", {"start": v(-2.84, -0.26) * mm, "end": v(-2.8, -0.55) * mm});
            skLineSegment(sketch, "E17.2.16.0", {"start": v(-3.08, -0.66) * mm, "end": v(-2.8, -0.58) * mm});
            skLineSegment(sketch, "E17.3.16.0", {"start": v(-3.08, -0.66) * mm, "end": v(-3, -0.95) * mm});
            skLineSegment(sketch, "E17.6.16.0", {"start": v(-3, -0.95) * mm, "end": v(-2.72, -0.87) * mm});
            skLineSegment(sketch, "E17.9.16.0", {"start": v(-2.8, -0.58) * mm, "end": v(-2.72, -0.87) * mm});
            skLineSegment(sketch, "E17.2.17.0", {"start": v(-2.99, -1) * mm, "end": v(-2.71, -0.9) * mm});
            skLineSegment(sketch, "E17.3.17.0", {"start": v(-2.99, -1) * mm, "end": v(-2.88, -1.28) * mm});
            skLineSegment(sketch, "E17.6.17.0", {"start": v(-2.88, -1.28) * mm, "end": v(-2.6, -1.17) * mm});
            skLineSegment(sketch, "E17.9.17.0", {"start": v(-2.71, -0.9) * mm, "end": v(-2.6, -1.17) * mm});
            skLineSegment(sketch, "E17.2.18.0", {"start": v(-2.86, -1.34) * mm, "end": v(-2.6, -1.2) * mm});
            skLineSegment(sketch, "E17.3.18.0", {"start": v(-2.86, -1.34) * mm, "end": v(-2.72, -1.6) * mm});
            skLineSegment(sketch, "E17.6.18.0", {"start": v(-2.72, -1.6) * mm, "end": v(-2.45, -1.46) * mm});
            skLineSegment(sketch, "E17.9.18.0", {"start": v(-2.6, -1.2) * mm, "end": v(-2.45, -1.46) * mm});
            skLineSegment(sketch, "E17.2.19.0", {"start": v(-2.68, -1.65) * mm, "end": v(-2.44, -1.48) * mm});
            skLineSegment(sketch, "E17.3.19.0", {"start": v(-2.68, -1.65) * mm, "end": v(-2.52, -1.9) * mm});
            skLineSegment(sketch, "E17.6.19.0", {"start": v(-2.52, -1.9) * mm, "end": v(-2.27, -1.73) * mm});
            skLineSegment(sketch, "E17.9.19.0", {"start": v(-2.44, -1.48) * mm, "end": v(-2.27, -1.73) * mm});
            skLineSegment(sketch, "E18.2.20.0", {"start": v(-2.48, -1.95) * mm, "end": v(-2.25, -1.75) * mm});
            skLineSegment(sketch, "E18.3.20.0", {"start": v(-2.48, -1.95) * mm, "end": v(-2.28, -2.18) * mm});
            skLineSegment(sketch, "E18.6.20.0", {"start": v(-2.28, -2.18) * mm, "end": v(-2.06, -1.98) * mm});
            skLineSegment(sketch, "E18.9.20.0", {"start": v(-2.25, -1.75) * mm, "end": v(-2.06, -1.98) * mm});
            skLineSegment(sketch, "E18.2.21.0", {"start": v(-2.24, -2.22) * mm, "end": v(-2.04, -2) * mm});
            skLineSegment(sketch, "E18.3.21.0", {"start": v(-2.24, -2.22) * mm, "end": v(-2.02, -2.42) * mm});
            skLineSegment(sketch, "E18.6.21.0", {"start": v(-2.02, -2.42) * mm, "end": v(-1.82, -2.2) * mm});
            skLineSegment(sketch, "E18.9.21.0", {"start": v(-2.04, -2) * mm, "end": v(-1.82, -2.2) * mm});
            skLineSegment(sketch, "E18.2.22.0", {"start": v(-1.97, -2.46) * mm, "end": v(-1.8, -2.22) * mm});
            skLineSegment(sketch, "E18.3.22.0", {"start": v(-1.97, -2.46) * mm, "end": v(-1.73, -2.64) * mm});
            skLineSegment(sketch, "E18.6.22.0", {"start": v(-1.73, -2.64) * mm, "end": v(-1.55, -2.4) * mm});
            skLineSegment(sketch, "E18.9.22.0", {"start": v(-1.8, -2.22) * mm, "end": v(-1.55, -2.4) * mm});
            skLineSegment(sketch, "E18.2.23.0", {"start": v(-1.68, -2.67) * mm, "end": v(-1.53, -2.4) * mm});
            skLineSegment(sketch, "E18.3.23.0", {"start": v(-1.68, -2.67) * mm, "end": v(-1.42, -2.82) * mm});
            skLineSegment(sketch, "E18.6.23.0", {"start": v(-1.42, -2.82) * mm, "end": v(-1.27, -2.56) * mm});
            skLineSegment(sketch, "E18.9.23.0", {"start": v(-1.53, -2.4) * mm, "end": v(-1.27, -2.56) * mm});
            skLineSegment(sketch, "E18.2.24.0", {"start": v(-1.36, -2.84) * mm, "end": v(-1.25, -2.57) * mm});
            skLineSegment(sketch, "E18.3.24.0", {"start": v(-1.36, -2.84) * mm, "end": v(-1.09, -2.96) * mm});
            skLineSegment(sketch, "E18.6.24.0", {"start": v(-1.09, -2.96) * mm, "end": v(-0.97, -2.68) * mm});
            skLineSegment(sketch, "E18.9.24.0", {"start": v(-1.25, -2.57) * mm, "end": v(-0.97, -2.68) * mm});
            skLineSegment(sketch, "E18.2.25.0", {"start": v(-1.03, -2.98) * mm, "end": v(-0.95, -2.7) * mm});
            skLineSegment(sketch, "E18.3.25.0", {"start": v(-1.03, -2.98) * mm, "end": v(-0.74, -3.06) * mm});
            skLineSegment(sketch, "E18.6.25.0", {"start": v(-0.74, -3.06) * mm, "end": v(-0.66, -2.78) * mm});
            skLineSegment(sketch, "E18.9.25.0", {"start": v(-0.95, -2.7) * mm, "end": v(-0.66, -2.78) * mm});
            skLineSegment(sketch, "E18.2.26.0", {"start": v(-0.68, -3.08) * mm, "end": v(-0.63, -2.78) * mm});
            skLineSegment(sketch, "E18.3.26.0", {"start": v(-0.68, -3.08) * mm, "end": v(-0.39, -3.13) * mm});
            skLineSegment(sketch, "E18.6.26.0", {"start": v(-0.39, -3.13) * mm, "end": v(-0.34, -2.83) * mm});
            skLineSegment(sketch, "E18.9.26.0", {"start": v(-0.63, -2.78) * mm, "end": v(-0.34, -2.83) * mm});
            skLineSegment(sketch, "E18.2.27.0", {"start": v(-0.33, -3.14) * mm, "end": v(-0.31, -2.84) * mm});
            skLineSegment(sketch, "E18.3.27.0", {"start": v(-0.33, -3.14) * mm, "end": v(-0.03, -3.15) * mm});
            skLineSegment(sketch, "E18.6.27.0", {"start": v(-0.03, -3.15) * mm, "end": v(-0.01, -2.85) * mm});
            skLineSegment(sketch, "E18.9.27.0", {"start": v(-0.31, -2.84) * mm, "end": v(-0.01, -2.85) * mm});
            skLineSegment(sketch, "E18.2.28.0", {"start": v(0.03, -3.15) * mm, "end": v(0.01, -2.85) * mm});
            skLineSegment(sketch, "E18.3.28.0", {"start": v(0.03, -3.15) * mm, "end": v(0.33, -3.14) * mm});
            skLineSegment(sketch, "E18.6.28.0", {"start": v(0.33, -3.14) * mm, "end": v(0.31, -2.84) * mm});
            skLineSegment(sketch, "E18.9.28.0", {"start": v(0.01, -2.85) * mm, "end": v(0.31, -2.84) * mm});
            skLineSegment(sketch, "E18.2.29.0", {"start": v(0.39, -3.13) * mm, "end": v(0.34, -2.83) * mm});
            skLineSegment(sketch, "E18.3.29.0", {"start": v(0.39, -3.13) * mm, "end": v(0.68, -3.08) * mm});
            skLineSegment(sketch, "E18.6.29.0", {"start": v(0.68, -3.08) * mm, "end": v(0.63, -2.78) * mm});
            skLineSegment(sketch, "E18.9.29.0", {"start": v(0.34, -2.83) * mm, "end": v(0.63, -2.78) * mm});
            skLineSegment(sketch, "E19.2.30.0", {"start": v(0.74, -3.06) * mm, "end": v(0.66, -2.78) * mm});
            skLineSegment(sketch, "E19.3.30.0", {"start": v(0.74, -3.06) * mm, "end": v(1.03, -2.98) * mm});
            skLineSegment(sketch, "E19.6.30.0", {"start": v(1.03, -2.98) * mm, "end": v(0.95, -2.7) * mm});
            skLineSegment(sketch, "E19.9.30.0", {"start": v(0.66, -2.78) * mm, "end": v(0.95, -2.7) * mm});
            skLineSegment(sketch, "E19.2.31.0", {"start": v(1.09, -2.96) * mm, "end": v(0.97, -2.68) * mm});
            skLineSegment(sketch, "E19.3.31.0", {"start": v(1.09, -2.96) * mm, "end": v(1.36, -2.84) * mm});
            skLineSegment(sketch, "E19.6.31.0", {"start": v(1.36, -2.84) * mm, "end": v(1.25, -2.57) * mm});
            skLineSegment(sketch, "E19.9.31.0", {"start": v(0.97, -2.68) * mm, "end": v(1.25, -2.57) * mm});
            skLineSegment(sketch, "E19.2.32.0", {"start": v(1.42, -2.82) * mm, "end": v(1.27, -2.56) * mm});
            skLineSegment(sketch, "E19.3.32.0", {"start": v(1.42, -2.82) * mm, "end": v(1.68, -2.67) * mm});
            skLineSegment(sketch, "E19.6.32.0", {"start": v(1.68, -2.67) * mm, "end": v(1.53, -2.4) * mm});
            skLineSegment(sketch, "E19.9.32.0", {"start": v(1.27, -2.56) * mm, "end": v(1.53, -2.4) * mm});
            skLineSegment(sketch, "E19.2.33.0", {"start": v(1.73, -2.64) * mm, "end": v(1.55, -2.4) * mm});
            skLineSegment(sketch, "E19.3.33.0", {"start": v(1.73, -2.64) * mm, "end": v(1.97, -2.46) * mm});
            skLineSegment(sketch, "E19.6.33.0", {"start": v(1.97, -2.46) * mm, "end": v(1.8, -2.22) * mm});
            skLineSegment(sketch, "E19.9.33.0", {"start": v(1.55, -2.4) * mm, "end": v(1.8, -2.22) * mm});
            skLineSegment(sketch, "E19.2.34.0", {"start": v(2.02, -2.42) * mm, "end": v(1.82, -2.2) * mm});
            skLineSegment(sketch, "E19.3.34.0", {"start": v(2.02, -2.42) * mm, "end": v(2.24, -2.22) * mm});
            skLineSegment(sketch, "E19.6.34.0", {"start": v(2.24, -2.22) * mm, "end": v(2.04, -2) * mm});
            skLineSegment(sketch, "E19.9.34.0", {"start": v(1.82, -2.2) * mm, "end": v(2.04, -2) * mm});
            skLineSegment(sketch, "E19.2.35.0", {"start": v(2.28, -2.18) * mm, "end": v(2.06, -1.98) * mm});
            skLineSegment(sketch, "E19.3.35.0", {"start": v(2.28, -2.18) * mm, "end": v(2.48, -1.95) * mm});
            skLineSegment(sketch, "E19.6.35.0", {"start": v(2.48, -1.95) * mm, "end": v(2.25, -1.75) * mm});
            skLineSegment(sketch, "E19.9.35.0", {"start": v(2.06, -1.98) * mm, "end": v(2.25, -1.75) * mm});
            skLineSegment(sketch, "E19.2.36.0", {"start": v(2.52, -1.9) * mm, "end": v(2.27, -1.73) * mm});
            skLineSegment(sketch, "E19.3.36.0", {"start": v(2.52, -1.9) * mm, "end": v(2.68, -1.65) * mm});
            skLineSegment(sketch, "E19.6.36.0", {"start": v(2.68, -1.65) * mm, "end": v(2.44, -1.48) * mm});
            skLineSegment(sketch, "E19.9.36.0", {"start": v(2.27, -1.73) * mm, "end": v(2.44, -1.48) * mm});
            skLineSegment(sketch, "E19.2.37.0", {"start": v(2.72, -1.6) * mm, "end": v(2.45, -1.46) * mm});
            skLineSegment(sketch, "E19.3.37.0", {"start": v(2.72, -1.6) * mm, "end": v(2.86, -1.34) * mm});
            skLineSegment(sketch, "E19.6.37.0", {"start": v(2.86, -1.34) * mm, "end": v(2.6, -1.2) * mm});
            skLineSegment(sketch, "E19.9.37.0", {"start": v(2.45, -1.46) * mm, "end": v(2.6, -1.2) * mm});
            skLineSegment(sketch, "E19.2.38.0", {"start": v(2.88, -1.28) * mm, "end": v(2.6, -1.17) * mm});
            skLineSegment(sketch, "E19.3.38.0", {"start": v(2.88, -1.28) * mm, "end": v(2.99, -1) * mm});
            skLineSegment(sketch, "E19.6.38.0", {"start": v(2.99, -1) * mm, "end": v(2.71, -0.9) * mm});
            skLineSegment(sketch, "E19.9.38.0", {"start": v(2.6, -1.17) * mm, "end": v(2.71, -0.9) * mm});
            skLineSegment(sketch, "E19.2.39.0", {"start": v(3, -0.95) * mm, "end": v(2.72, -0.87) * mm});
            skLineSegment(sketch, "E19.3.39.0", {"start": v(3, -0.95) * mm, "end": v(3.08, -0.66) * mm});
            skLineSegment(sketch, "E19.6.39.0", {"start": v(3.08, -0.66) * mm, "end": v(2.8, -0.58) * mm});
            skLineSegment(sketch, "E19.9.39.0", {"start": v(2.72, -0.87) * mm, "end": v(2.8, -0.58) * mm});
            skLineSegment(sketch, "E20.2.40.0", {"start": v(3.1, -0.6) * mm, "end": v(2.8, -0.55) * mm});
            skLineSegment(sketch, "E20.3.40.0", {"start": v(3.1, -0.6) * mm, "end": v(3.14, -0.3) * mm});
            skLineSegment(sketch, "E20.6.40.0", {"start": v(3.14, -0.3) * mm, "end": v(2.84, -0.26) * mm});
            skLineSegment(sketch, "E20.9.40.0", {"start": v(2.8, -0.55) * mm, "end": v(2.84, -0.26) * mm});
            skLineSegment(sketch, "E20.2.41.0", {"start": v(3.14, -0.24) * mm, "end": v(2.84, -0.23) * mm});
            skLineSegment(sketch, "E20.3.41.0", {"start": v(3.14, -0.24) * mm, "end": v(3.15, 0.06) * mm});
            skLineSegment(sketch, "E20.6.41.0", {"start": v(3.15, 0.06) * mm, "end": v(2.85, 0.07) * mm});
            skLineSegment(sketch, "E20.9.41.0", {"start": v(2.84, -0.23) * mm, "end": v(2.85, 0.07) * mm});
            skLineSegment(sketch, "E20.2.42.0", {"start": v(3.15, 0.12) * mm, "end": v(2.85, 0.1) * mm});
            skLineSegment(sketch, "E20.3.42.0", {"start": v(3.15, 0.12) * mm, "end": v(3.13, 0.42) * mm});
            skLineSegment(sketch, "E20.6.42.0", {"start": v(3.13, 0.42) * mm, "end": v(2.83, 0.4) * mm});
            skLineSegment(sketch, "E20.9.42.0", {"start": v(2.85, 0.1) * mm, "end": v(2.83, 0.4) * mm});
            skLineSegment(sketch, "E20.2.43.0", {"start": v(3.12, 0.48) * mm, "end": v(2.82, 0.42) * mm});
            skLineSegment(sketch, "E20.3.43.0", {"start": v(3.12, 0.48) * mm, "end": v(3.06, 0.77) * mm});
            skLineSegment(sketch, "E20.6.43.0", {"start": v(3.06, 0.77) * mm, "end": v(2.76, 0.71) * mm});
            skLineSegment(sketch, "E20.9.43.0", {"start": v(2.82, 0.42) * mm, "end": v(2.76, 0.71) * mm});
            skLineSegment(sketch, "E20.2.44.0", {"start": v(3.04, 0.83) * mm, "end": v(2.76, 0.74) * mm});
            skLineSegment(sketch, "E20.3.44.0", {"start": v(3.04, 0.83) * mm, "end": v(2.95, 1.12) * mm});
            skLineSegment(sketch, "E20.6.44.0", {"start": v(2.95, 1.12) * mm, "end": v(2.66, 1.02) * mm});
            skLineSegment(sketch, "E20.9.44.0", {"start": v(2.76, 0.74) * mm, "end": v(2.66, 1.02) * mm});
            skLineSegment(sketch, "E20.2.45.0", {"start": v(2.93, 1.17) * mm, "end": v(2.65, 1.05) * mm});
            skLineSegment(sketch, "E20.3.45.0", {"start": v(2.93, 1.17) * mm, "end": v(2.8, 1.45) * mm});
            skLineSegment(sketch, "E20.6.45.0", {"start": v(2.8, 1.45) * mm, "end": v(2.53, 1.32) * mm});
            skLineSegment(sketch, "E20.9.45.0", {"start": v(2.65, 1.05) * mm, "end": v(2.53, 1.32) * mm});
            skLineSegment(sketch, "E20.2.46.0", {"start": v(2.77, 1.5) * mm, "end": v(2.52, 1.34) * mm});
            skLineSegment(sketch, "E20.3.46.0", {"start": v(2.77, 1.5) * mm, "end": v(2.62, 1.76) * mm});
            skLineSegment(sketch, "E20.6.46.0", {"start": v(2.62, 1.76) * mm, "end": v(2.36, 1.6) * mm});
            skLineSegment(sketch, "E20.9.46.0", {"start": v(2.52, 1.34) * mm, "end": v(2.36, 1.6) * mm});
            skLineSegment(sketch, "E20.2.47.0", {"start": v(2.59, 1.8) * mm, "end": v(2.35, 1.62) * mm});
            skLineSegment(sketch, "E20.3.47.0", {"start": v(2.59, 1.8) * mm, "end": v(2.4, 2.04) * mm});
            skLineSegment(sketch, "E20.6.47.0", {"start": v(2.4, 2.04) * mm, "end": v(2.17, 1.86) * mm});
            skLineSegment(sketch, "E20.9.47.0", {"start": v(2.35, 1.62) * mm, "end": v(2.17, 1.86) * mm});
            skLineSegment(sketch, "E20.2.48.0", {"start": v(2.36, 2.09) * mm, "end": v(2.15, 1.88) * mm});
            skLineSegment(sketch, "E20.3.48.0", {"start": v(2.36, 2.09) * mm, "end": v(2.15, 2.3) * mm});
            skLineSegment(sketch, "E20.6.48.0", {"start": v(2.15, 2.3) * mm, "end": v(1.94, 2.1) * mm});
            skLineSegment(sketch, "E20.9.48.0", {"start": v(2.15, 1.88) * mm, "end": v(1.94, 2.1) * mm});
            skLineSegment(sketch, "E20.2.49.0", {"start": v(2.11, 2.34) * mm, "end": v(1.92, 2.11) * mm});
            skLineSegment(sketch, "E20.3.49.0", {"start": v(2.11, 2.34) * mm, "end": v(1.88, 2.53) * mm});
            skLineSegment(sketch, "E20.6.49.0", {"start": v(1.88, 2.53) * mm, "end": v(1.69, 2.3) * mm});
            skLineSegment(sketch, "E20.9.49.0", {"start": v(1.92, 2.11) * mm, "end": v(1.69, 2.3) * mm});
            skLineSegment(sketch, "E21.2.50.0", {"start": v(1.83, 2.57) * mm, "end": v(1.67, 2.32) * mm});
            skLineSegment(sketch, "E21.3.50.0", {"start": v(1.83, 2.57) * mm, "end": v(1.58, 2.73) * mm});
            skLineSegment(sketch, "E21.6.50.0", {"start": v(1.58, 2.73) * mm, "end": v(1.41, 2.48) * mm});
            skLineSegment(sketch, "E21.9.50.0", {"start": v(1.67, 2.32) * mm, "end": v(1.41, 2.48) * mm});
            skLineSegment(sketch, "E21.2.51.0", {"start": v(1.52, 2.76) * mm, "end": v(1.4, 2.5) * mm});
            skLineSegment(sketch, "E21.3.51.0", {"start": v(1.52, 2.76) * mm, "end": v(1.26, 2.9) * mm});
            skLineSegment(sketch, "E21.6.51.0", {"start": v(1.26, 2.9) * mm, "end": v(1.12, 2.62) * mm});
            skLineSegment(sketch, "E21.9.51.0", {"start": v(1.4, 2.5) * mm, "end": v(1.12, 2.62) * mm});
            skLineSegment(sketch, "E21.2.52.0", {"start": v(1.2, 2.92) * mm, "end": v(1.1, 2.63) * mm});
            skLineSegment(sketch, "E21.3.52.0", {"start": v(1.2, 2.92) * mm, "end": v(0.92, 3.02) * mm});
            skLineSegment(sketch, "E21.6.52.0", {"start": v(0.92, 3.02) * mm, "end": v(0.82, 2.73) * mm});
            skLineSegment(sketch, "E21.9.52.0", {"start": v(1.1, 2.63) * mm, "end": v(0.82, 2.73) * mm});
            skLineSegment(sketch, "E21.2.53.0", {"start": v(0.86, 3.03) * mm, "end": v(0.8, 2.74) * mm});
            skLineSegment(sketch, "E21.3.53.0", {"start": v(0.86, 3.03) * mm, "end": v(0.57, 3.1) * mm});
            skLineSegment(sketch, "E21.6.53.0", {"start": v(0.57, 3.1) * mm, "end": v(0.5, 2.8) * mm});
            skLineSegment(sketch, "E21.9.53.0", {"start": v(0.8, 2.74) * mm, "end": v(0.5, 2.8) * mm});
            skLineSegment(sketch, "E21.2.54.0", {"start": v(0.5, 3.11) * mm, "end": v(0.47, 2.81) * mm});
            skLineSegment(sketch, "E21.3.54.0", {"start": v(0.5, 3.11) * mm, "end": v(0.21, 3.15) * mm});
            skLineSegment(sketch, "E21.6.54.0", {"start": v(0.21, 3.15) * mm, "end": v(0.18, 2.85) * mm});
            skLineSegment(sketch, "E21.9.54.0", {"start": v(0.47, 2.81) * mm, "end": v(0.18, 2.85) * mm});
            skSolve(sketch);
        }
        {
            var Q0;
            Q0 = qSketchRegion(id + "F6", true);
            extrude(context, id + "F7", {"entities" : qUnion([Q0]), "operationType" : NewBodyOperationType.ADD, "oppositeDirection" : true, "depth" : 5 * mm});
        }
    });
